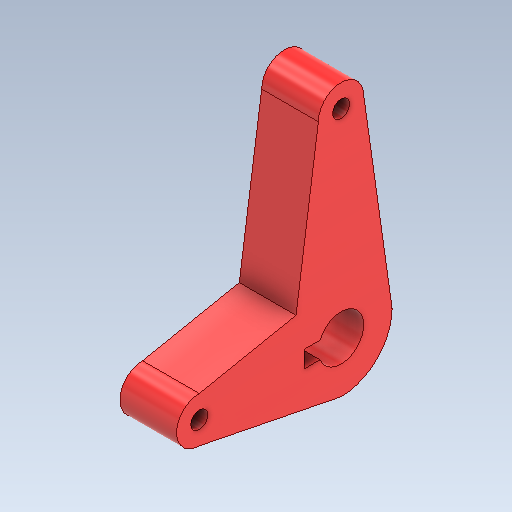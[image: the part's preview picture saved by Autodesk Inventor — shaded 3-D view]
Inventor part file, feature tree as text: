
AUTODESK INVENTOR PART (.ipt)
format: ipt  version: 2021 (Build 250183000, 183)  size: 137,216 bytes
history: native  units: in
note: dims shown in document units (in); Inventor stores cm internally (conversion verified against a paired STEP export)
features: sketch x4, extrude x1
ambient origin geometry x8: Origin, YZ Plane, XZ Plane, XY Plane, X Axis, Y Axis, Z Axis, Center Point
bodies: Solid1 (feature_tree)
feature tree (5):
  sketch  "Sketch1"  dims[d0=1.4173in d1=0.6299in]
  sketch  "Sketch2"  dims[d2=2.7559in]
  sketch  "Sketch3"  dims[d3=0.2362in]
  sketch  "Sketch4"  dims[d4=0.6299in d5=1.9685in d6=0.2362in d7=0.6299in d14=0.1969in d15=0.1181in d16=0.1181in d17=0.3937in d18=0.3937in d19=0.0in d20=0.0in]
  extrude  "Extrusion1"  Depth=0.6299in
